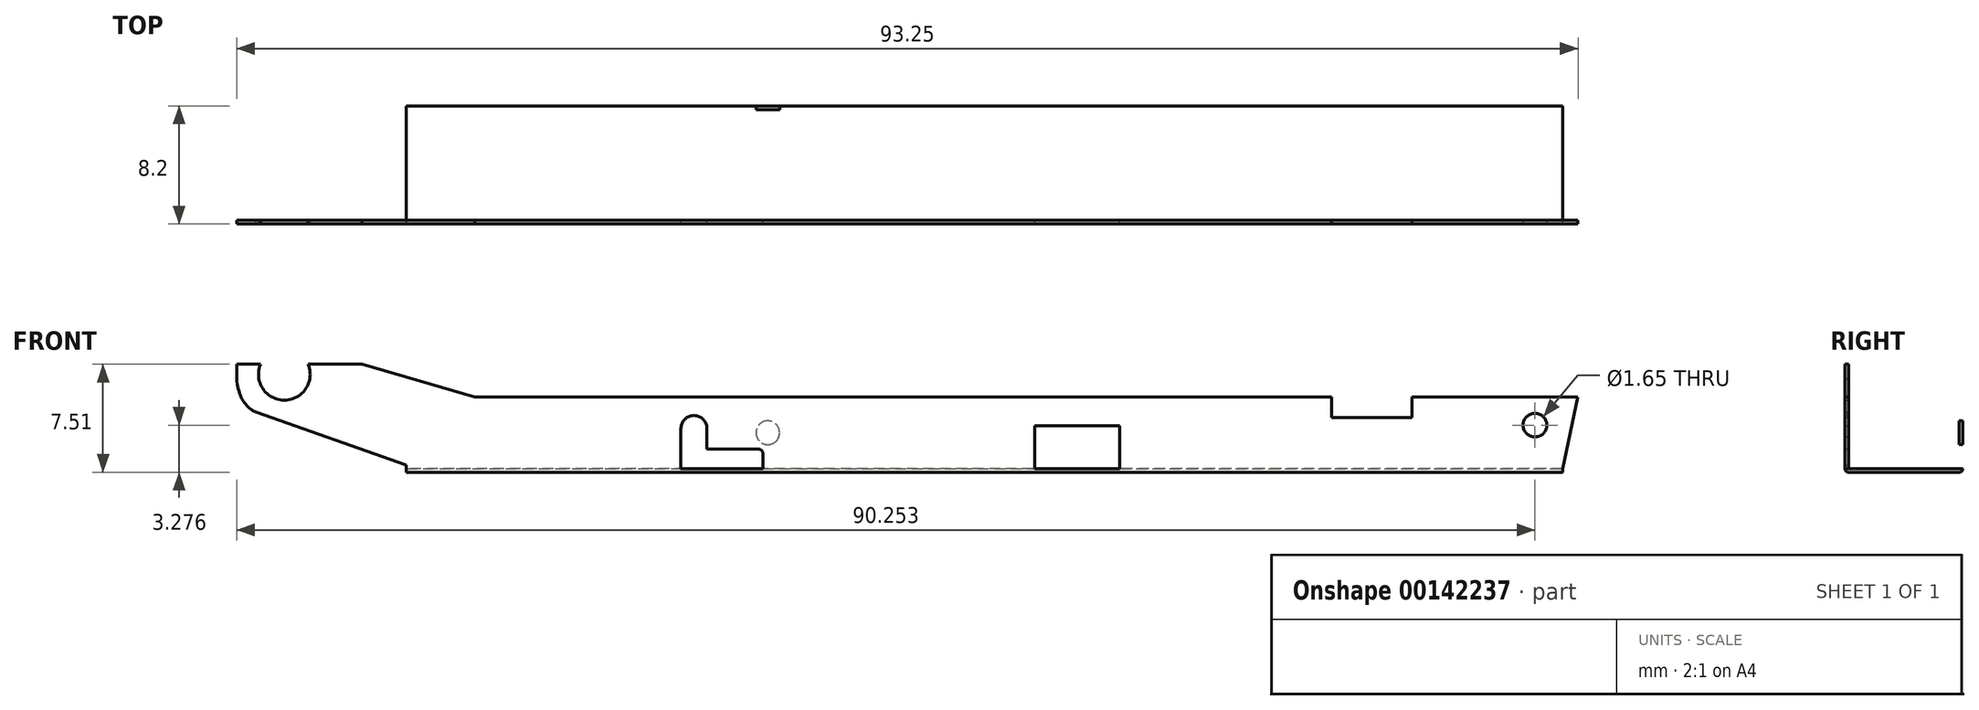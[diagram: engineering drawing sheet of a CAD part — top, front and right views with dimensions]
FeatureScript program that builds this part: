
annotation { "Feature Type Name" : "Feature", "Feature Type Description" : "" }
export const myFeature = defineFeature(function(context is Context, id is Id, definition is map)
    precondition{}
    {
        {
            var Q0;
            Q0=qCreatedBy(makeId("Front.planeOp"),FACE);
            var sketch = newSketch(context, id + "F0", { "sketchPlane" : qUnion([Q0])});
            skLineSegment(sketch, "E0", {"start": v(-40.19, 0) * mm, "end": v(40.19, 0) * mm});
            skLineSegment(sketch, "E1", {"start": v(-40.19, 0) * mm, "end": v(-40.19, 0.25) * mm});
            skLineSegment(sketch, "E2", {"start": v(-40.19, 0) * mm, "end": v(-51.99, 0) * mm, "construction": true});
            skLineSegment(sketch, "E3", {"start": v(-51.99, 0) * mm, "end": v(-51.99, 7.26) * mm});
            skLineSegment(sketch, "E4", {"start": v(-51.99, 7.26) * mm, "end": v(-50.33, 7.26) * mm});
            skPoint(sketch, "E5", {"position": v(-50.33, 7.26) * mm});
            skPoint(sketch, "E6", {"position": v(-47.03, 7.26) * mm});
            skArc(sketch, "E7", {"start": v(-50.33, 7.26) * mm, "mid": v(-48.67, 4.76) * mm, "end": v(-47.03, 7.26) * mm});
            skPoint(sketch, "E8", {"position": v(-48.68, 4.76) * mm});
            skLineSegment(sketch, "E9", {"start": v(-43.27, 7.26) * mm, "end": v(-43.27, 5) * mm, "construction": true});
            skLineSegment(sketch, "E10", {"start": v(-43.27, 5) * mm, "end": v(-35.45, 5) * mm, "construction": true});
            skLineSegment(sketch, "E11", {"start": v(-43.27, 7.26) * mm, "end": v(-35.45, 5) * mm});
            skLineSegment(sketch, "E12", {"start": v(-35.45, 5) * mm, "end": v(24.12, 5) * mm});
            skLineSegment(sketch, "E13", {"start": v(41.26, 5) * mm, "end": v(40.19, 0) * mm});
            skLineSegment(sketch, "E14", {"start": v(-40.18, 0.25) * mm, "end": v(-50.66, 3.94) * mm});
            skFitSpline(sketch, "E15", {"points": [v(-51.99, 7.26) * mm, v(-50.66, 3.94) * mm], "startDerivative": vector(-0.48, -6.82) * mm, "endDerivative": vector(1.78, -0.73) * mm});
            skLineSegment(sketch, "E16", {"start": v(-52.15, 4.99) * mm, "end": v(-51.99, 4.99) * mm});
            skLineSegment(sketch, "E17", {"start": v(-51.25, 4.18) * mm, "end": v(-51.99, 4.18) * mm});
            skLineSegment(sketch, "E18", {"start": v(-51.25, 4.18) * mm, "end": v(-50.66, 3.94) * mm});
            skPoint(sketch, "E19", {"position": v(29.7, 5) * mm});
            skPoint(sketch, "E20", {"position": v(24.12, 5) * mm});
            skLineSegment(sketch, "E21", {"start": v(29.7, 5) * mm, "end": v(29.7, 3.55) * mm});
            skLineSegment(sketch, "E22", {"start": v(24.12, 5) * mm, "end": v(24.12, 3.55) * mm});
            skLineSegment(sketch, "E23", {"start": v(24.12, 3.55) * mm, "end": v(29.7, 3.55) * mm});
            skLineSegment(sketch, "E24.trimOffspring", {"start": v(29.7, 5) * mm, "end": v(41.26, 5) * mm});
            skLineSegment(sketch, "E25.trimOffspring", {"start": v(-47.03, 7.26) * mm, "end": v(-43.27, 7.26) * mm});
            skLineSegment(sketch, "E26", {"start": v(-40.19, 0) * mm, "end": v(3.5, 0) * mm});
            skPoint(sketch, "E27", {"position": v(9.4, 0) * mm});
            skLineSegment(sketch, "E28", {"start": v(3.5, 0) * mm, "end": v(3.5, 2.98) * mm});
            skLineSegment(sketch, "E29", {"start": v(3.5, 2.98) * mm, "end": v(9.4, 2.98) * mm});
            skLineSegment(sketch, "E30", {"start": v(9.4, 2.98) * mm, "end": v(9.4, 0) * mm});
            skPoint(sketch, "E31", {"position": v(-21.1, 0) * mm});
            skPoint(sketch, "E32", {"position": v(-15.4, 0) * mm});
            skLineSegment(sketch, "E33", {"start": v(-21.1, 0) * mm, "end": v(-21.1, 2.8) * mm});
            skLineSegment(sketch, "E34", {"start": v(-15.4, 0) * mm, "end": v(-15.4, 1.04) * mm});
            skLineSegment(sketch, "E35", {"start": v(-15.73, 1.37) * mm, "end": v(-19.3, 1.37) * mm});
            skLineSegment(sketch, "E36", {"start": v(-19.3, 1.37) * mm, "end": v(-19.3, 2.8) * mm});
            skArc(sketch, "E37", {"start": v(-19.3, 2.8) * mm, "mid": v(-20.2, 3.7) * mm, "end": v(-21.1, 2.8) * mm});
            skPoint(sketch, "E38.visualSharp", {"position": v(-15.4, 1.37) * mm});
            skArc(sketch, "E38.filletArc", {"start": v(-15.4, 1.04) * mm, "mid": v(-15.5, 1.27) * mm, "end": v(-15.73, 1.37) * mm});
            skSolve(sketch);
        }
        {
            var Q0;
            Q0=qCreatedBy(makeId("Front.planeOp"),FACE);
            cPlane(context, id + "F1", {"entities" : qUnion([Q0]), "cplaneType" : CPlaneType.OFFSET, "offset" : 7.7 * mm, "oppositeDirection" : true, "width" : 150 * mm, "height" : 150 * mm});
        }
        {
            var Q0;
            Q0=qCreatedBy(id+"F1.planeOp",FACE);
            var sketch = newSketch(context, id + "F2", { "sketchPlane" : qUnion([Q0])});
            skLineSegment(sketch, "E39.0.0", {"start": v(9.4, 2.98) * mm, "end": v(9.4, 0) * mm});
            skLineSegment(sketch, "E39.0.1", {"start": v(9.4, 0) * mm, "end": v(40.19, 0) * mm});
            skLineSegment(sketch, "E39.0.2", {"start": v(40.19, 0) * mm, "end": v(41.26, 5) * mm});
            skLineSegment(sketch, "E39.0.3", {"start": v(41.26, 5) * mm, "end": v(29.7, 5) * mm});
            skLineSegment(sketch, "E39.0.4", {"start": v(29.7, 5) * mm, "end": v(29.7, 3.55) * mm});
            skLineSegment(sketch, "E39.0.5", {"start": v(29.7, 3.55) * mm, "end": v(24.12, 3.55) * mm});
            skLineSegment(sketch, "E39.0.6", {"start": v(24.12, 3.55) * mm, "end": v(24.12, 5) * mm});
            skLineSegment(sketch, "E39.0.7", {"start": v(24.12, 5) * mm, "end": v(-35.45, 5) * mm});
            skLineSegment(sketch, "E39.0.8", {"start": v(-35.45, 5) * mm, "end": v(-43.27, 7.26) * mm});
            skLineSegment(sketch, "E39.0.9", {"start": v(-43.27, 7.26) * mm, "end": v(-47.03, 7.26) * mm});
            skArc(sketch, "E39.0.10", {"start": v(-47.03, 7.26) * mm, "mid": v(-48.68, 4.76) * mm, "end": v(-50.33, 7.26) * mm});
            skLineSegment(sketch, "E39.0.11", {"start": v(-50.33, 7.26) * mm, "end": v(-51.99, 7.26) * mm});
            skLineSegment(sketch, "E39.0.12", {"start": v(-51.99, 7.26) * mm, "end": v(-51.99, 6.26) * mm});
            skFitSpline(sketch, "E39.0.13", {"points": [v(-51.99, 7.26) * mm, v(-52.15, 4.99) * mm, v(-51.25, 4.18) * mm, v(-50.66, 3.94) * mm]});
            skLineSegment(sketch, "E39.0.14", {"start": v(-50.66, 3.94) * mm, "end": v(-40.18, 0.25) * mm});
            skLineSegment(sketch, "E39.0.15", {"start": v(-40.19, 0.25) * mm, "end": v(-40.19, 0) * mm});
            skLineSegment(sketch, "E39.0.16", {"start": v(-40.19, 0) * mm, "end": v(-21.1, 0) * mm});
            skLineSegment(sketch, "E39.0.23", {"start": v(-15.4, 0) * mm, "end": v(3.5, 0) * mm});
            skLineSegment(sketch, "E39.0.24", {"start": v(3.5, 0) * mm, "end": v(3.5, 2.98) * mm});
            skLineSegment(sketch, "E39.0.25", {"start": v(3.5, 2.98) * mm, "end": v(9.4, 2.98) * mm});
            skLineSegment(sketch, "E40.0", {"start": v(-40.19, 0) * mm, "end": v(3.5, 0) * mm});
            skLineSegment(sketch, "E41.0", {"start": v(-40.19, 0) * mm, "end": v(40.19, 0) * mm});
            skSolve(sketch);
        }
        {
            var Q0;
            {var subQ5=sQuery(id+"F0.wireOp",EDGE,"E1");Q0=makeQuery(id+"F0.imprint","IMPRINT",FACE,{"disambiguationData":[TD([[makeQuery(id+"F0.imprint","IMPRINT",EDGE,{"derivedFrom":subQ5}),-1.0]])]});}
            extrude(context, id + "F3", {"entities" : qUnion([Q0]), "depth" : 0.25 * mm});
        }
        {
            var Q0;
            {var subQ4=sQuery(id+"F2.wireOp",EDGE,"E39.0.0");Q0=makeQuery(id+"F2.imprint","IMPRINT",FACE,{"disambiguationData":[TD([[makeQuery(id+"F2.imprint","IMPRINT",EDGE,{"derivedFrom":subQ4}),1.0]])]});}
            extrude(context, id + "F4", {"entities" : qUnion([Q0]), "oppositeDirection" : true, "depth" : 0.25 * mm});
        }
        {
            var Q0;
            Q0=qCreatedBy(makeId("Top.planeOp"),FACE);
            var sketch = newSketch(context, id + "F5", { "sketchPlane" : qUnion([Q0])});
            skPoint(sketch, "E42.0", {"position": v(40.19, 0) * mm});
            skPoint(sketch, "E43.0", {"position": v(40.19, 7.7) * mm});
            skPoint(sketch, "E44.0", {"position": v(-40.19, 0) * mm});
            skPoint(sketch, "E45.0", {"position": v(-40.18, 7.7) * mm});
            skLineSegment(sketch, "E46.bottom", {"start": v(40.18, 0) * mm, "end": v(-40.18, 0) * mm});
            skLineSegment(sketch, "E46.top", {"start": v(40.18, 7.7) * mm, "end": v(-40.18, 7.7) * mm});
            skLineSegment(sketch, "E46.left", {"start": v(40.19, 0) * mm, "end": v(40.19, 7.7) * mm});
            skLineSegment(sketch, "E46.right", {"start": v(-40.18, 0) * mm, "end": v(-40.18, 7.7) * mm});
            skSolve(sketch);
        }
        {
            var Q0;
            Q0=makeQuery(id+"F5.imprint","IMPRINT",FACE,{"disambiguationData":[TD([[makeQuery(id+"F5.imprint","IMPRINT",EDGE,{"derivedFrom":sQuery(id+"F5.wireOp",EDGE,"E46.bottom")}),-1.0]])]});
            extrude(context, id + "F6", {"entities" : qUnion([Q0]), "oppositeDirection" : true, "depth" : 0.25 * mm});
        }
        {
            var Q0;
            Q0=makeQuery(id+"F6.opExtrude","SWEPT_FACE",FACE,{"disambiguationData":[OSD([sQuery(id+"F5.wireOp",EDGE,"E46.right")])]});
            var sketch = newSketch(context, id + "F7", { "sketchPlane" : qUnion([Q0])});
            skPoint(sketch, "E47.0", {"position": v(0.25, 0) * mm});
            skPoint(sketch, "E48.0", {"position": v(0, -0.25) * mm});
            skArc(sketch, "E49", {"start": v(0, -0.25) * mm, "mid": v(0.18, -0.18) * mm, "end": v(0.25, 0) * mm});
            skLineSegment(sketch, "E50", {"start": v(0.25, 0) * mm, "end": v(0, 0) * mm});
            skLineSegment(sketch, "E51", {"start": v(0, 0) * mm, "end": v(0, -0.25) * mm});
            skSolve(sketch);
        }
        {
            var Q0;
            Q0=makeQuery(id+"F7.imprint","IMPRINT",FACE,{"disambiguationData":[TD([[makeQuery(id+"F7.imprint","IMPRINT",EDGE,{"derivedFrom":sQuery(id+"F7.wireOp",EDGE,"E49")}),1.0]])]});
            var Q1;
            Q1=qConstructionFilter(qBodyType(qCreatedBy(id+"F7",EDGE),BodyType.WIRE),ConstructionObject.NO);
            var Q2;
            Q2=makeQuery(id+"F6.opExtrude","SWEPT_FACE",FACE,{"disambiguationData":[OSD([sQuery(id+"F5.wireOp",EDGE,"E46.left")])]});
            extrude(context, id + "F8", {"entities" : qUnion([Q0]), "operationType" : NewBodyOperationType.ADD, "surfaceEntities" : qUnion([Q1]), "endBound" : BoundingType.UP_TO_SURFACE, "oppositeDirection" : true, "endBoundEntityFace" : qUnion([Q2]), "depth" : 1.77 * mm});
        }
        {
            var Q0;
            Q0=makeQuery(id+"F6.opExtrude","SWEPT_FACE",FACE,{"disambiguationData":[OSD([sQuery(id+"F5.wireOp",EDGE,"E46.right")])]});
            var sketch = newSketch(context, id + "F9", { "sketchPlane" : qUnion([Q0])});
            skPoint(sketch, "E52.0", {"position": v(-7.95, 0) * mm});
            skArc(sketch, "E53", {"start": v(-7.95, 0) * mm, "mid": v(-7.88, -0.18) * mm, "end": v(-7.7, -0.25) * mm});
            skLineSegment(sketch, "E54", {"start": v(-7.7, 0) * mm, "end": v(-7.95, 0) * mm});
            skLineSegment(sketch, "E55", {"start": v(-7.7, 0) * mm, "end": v(-7.7, -0.25) * mm});
            skSolve(sketch);
        }
        {
            var Q0;
            Q0=makeQuery(id+"F9.imprint","IMPRINT",FACE,{"disambiguationData":[TD([[makeQuery(id+"F9.imprint","IMPRINT",EDGE,{"derivedFrom":sQuery(id+"F9.wireOp",EDGE,"E53")}),1.0]])]});
            var Q1;
            Q1=makeQuery(id+"F6.opExtrude","SWEPT_FACE",FACE,{"disambiguationData":[OSD([sQuery(id+"F5.wireOp",EDGE,"E46.left")])]});
            extrude(context, id + "F10", {"entities" : qUnion([Q0]), "operationType" : NewBodyOperationType.ADD, "endBound" : BoundingType.UP_TO_SURFACE, "oppositeDirection" : true, "endBoundEntityFace" : qUnion([Q1]), "depth" : 25 * mm});
        }
        {
            var Q0;
            Q0=makeQuery(id+"F3.opExtrude","CAP_FACE",FACE,{"disambiguationData":[OSD([sQuery(id+"F0.wireOp",EDGE,"E0"),sQuery(id+"F0.wireOp",EDGE,"E1"),sQuery(id+"F0.wireOp",EDGE,"E3"),sQuery(id+"F0.wireOp",EDGE,"E4"),sQuery(id+"F0.wireOp",EDGE,"E7"),sQuery(id+"F0.wireOp",EDGE,"E11"),sQuery(id+"F0.wireOp",EDGE,"E12"),sQuery(id+"F0.wireOp",EDGE,"E13"),sQuery(id+"F0.wireOp",EDGE,"E14"),sQuery(id+"F0.wireOp",EDGE,"E15"),sQuery(id+"F0.wireOp",EDGE,"E21"),sQuery(id+"F0.wireOp",EDGE,"E22"),sQuery(id+"F0.wireOp",EDGE,"E23"),sQuery(id+"F0.wireOp",EDGE,"E24.trimOffspring"),sQuery(id+"F0.wireOp",EDGE,"E25.trimOffspring"),sQuery(id+"F0.wireOp",EDGE,"E26"),sQuery(id+"F0.wireOp",EDGE,"E28"),sQuery(id+"F0.wireOp",EDGE,"E29"),sQuery(id+"F0.wireOp",EDGE,"E30"),sQuery(id+"F0.wireOp",EDGE,"E33"),sQuery(id+"F0.wireOp",EDGE,"E34"),sQuery(id+"F0.wireOp",EDGE,"E35"),sQuery(id+"F0.wireOp",EDGE,"E36"),sQuery(id+"F0.wireOp",EDGE,"E37"),sQuery(id+"F0.wireOp",EDGE,"E38.filletArc")])],"isStart":false});
            var sketch = newSketch(context, id + "F11", { "sketchPlane" : qUnion([Q0])});
            skCircle(sketch, "E56", {"center": v(38.26, 3.03) * mm, "radius": 0.82 * mm});
            skLineSegment(sketch, "E57", {"start": v(38.26, 5) * mm, "end": v(38.26, 0) * mm});
            skCircle(sketch, "E58", {"center": v(-15.07, 2.5) * mm, "radius": 0.82 * mm});
            skLineSegment(sketch, "E59", {"start": v(-15.07, 5) * mm, "end": v(-15.07, 0) * mm});
            skSolve(sketch);
        }
        {
            var Q0;
            {var subQ0=sQuery(id+"F11.wireOp",EDGE,"E57");var subQ1=sQuery(id+"F11.wireOp",EDGE,"E56");var subQ2=makeQuery(id+"F11.imprint","INTERSECT",VERTEX,{"disambiguationData":[OD(0.0)],"derivedFrom":[subQ1,subQ0]});Q0=makeQuery(id+"F11.imprint","IMPRINT",FACE,{"disambiguationData":[TD([[makeQuery(id+"F11.imprint","IMPRINT",EDGE,{"disambiguationData":[TD([[subQ2,1.0]])],"derivedFrom":subQ1}),1.0]])]});}
            var Q1;
            {var subQ0=sQuery(id+"F11.wireOp",EDGE,"E57");var subQ1=sQuery(id+"F11.wireOp",EDGE,"E56");var subQ2=makeQuery(id+"F11.imprint","INTERSECT",VERTEX,{"disambiguationData":[OD(0.0)],"derivedFrom":[subQ1,subQ0]});Q1=makeQuery(id+"F11.imprint","IMPRINT",FACE,{"disambiguationData":[TD([[makeQuery(id+"F11.imprint","IMPRINT",EDGE,{"disambiguationData":[TD([[subQ2,-1.0]])],"derivedFrom":subQ1}),1.0]])]});}
            extrude(context, id + "F12", {"entities" : qUnion([Q0, Q1]), "operationType" : NewBodyOperationType.REMOVE, "endBound" : BoundingType.THROUGH_ALL, "oppositeDirection" : true, "depth" : 25 * mm});
        }
        {
            var Q0;
            Q0=makeQuery(id+"F4.opExtrude","CAP_FACE",FACE,{"disambiguationData":[OSD([sQuery(id+"F2.wireOp",EDGE,"E39.0.0"),sQuery(id+"F2.wireOp",EDGE,"E39.0.2"),sQuery(id+"F2.wireOp",EDGE,"E39.0.3"),sQuery(id+"F2.wireOp",EDGE,"E39.0.4"),sQuery(id+"F2.wireOp",EDGE,"E39.0.5"),sQuery(id+"F2.wireOp",EDGE,"E39.0.6"),sQuery(id+"F2.wireOp",EDGE,"E39.0.7"),sQuery(id+"F2.wireOp",EDGE,"E39.0.8"),sQuery(id+"F2.wireOp",EDGE,"E39.0.9"),sQuery(id+"F2.wireOp",EDGE,"E39.0.10"),sQuery(id+"F2.wireOp",EDGE,"E39.0.11"),sQuery(id+"F2.wireOp",EDGE,"E39.0.12"),sQuery(id+"F2.wireOp",EDGE,"E39.0.13"),sQuery(id+"F2.wireOp",EDGE,"E39.0.14"),sQuery(id+"F2.wireOp",EDGE,"E39.0.15"),sQuery(id+"F2.wireOp",EDGE,"E39.0.24"),sQuery(id+"F2.wireOp",EDGE,"E39.0.25"),sQuery(id+"F2.wireOp",EDGE,"E41.0")])],"isStart":false});
            var sketch = newSketch(context, id + "F13", { "sketchPlane" : qUnion([Q0])});
            skCircle(sketch, "E60.0", {"center": v(15.07, 2.5) * mm, "radius": 0.82 * mm});
            skSolve(sketch);
        }
        {
            var Q0;
            Q0=makeQuery(id+"F13.imprint","IMPRINT",FACE,{"disambiguationData":[TD([[makeQuery(id+"F13.imprint","IMPRINT",EDGE,{"derivedFrom":sQuery(id+"F13.wireOp",EDGE,"E60.0")}),-1.0]])]});
            extrude(context, id + "F14", {"entities" : qUnion([Q0]), "operationType" : NewBodyOperationType.REMOVE, "oppositeDirection" : true, "depth" : 2 * mm});
        }
    });
